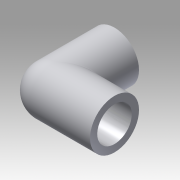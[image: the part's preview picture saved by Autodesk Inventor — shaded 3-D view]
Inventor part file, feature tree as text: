
AUTODESK INVENTOR PART (.ipt)
format: ipt  version: 2015 (Build 190159000, 159)  size: 176,128 bytes
history: native  units: in
note: dims shown in document units (in); Inventor stores cm internally (conversion verified against a paired STEP export)
features: fillet x3, sketch x2, sweep x1
ambient origin geometry x8: Origin, YZ Plane, XZ Plane, XY Plane, X Axis, Y Axis, Z Axis, Center Point
bodies: Solid1 (feature_tree)
feature tree (6):
  sweep  "Sweep1"
  fillet  "Fillet1"  Radius=0.375in
  fillet  "Fillet2"  Radius=0.0312in
  fillet  "Fillet3"  [1 undecoded]
  sketch  "Sketch1"  dims[d0=0.0in d1=0.0in d2=0.5in d3=0.375in d4=0.0312in]
  sketch  "Sketch2"
note: 1 required parameter value undecoded (feature->parameter linkage not recoverable at this tier; creation-order binding heuristic only, values carry confidence <= 0.55)
